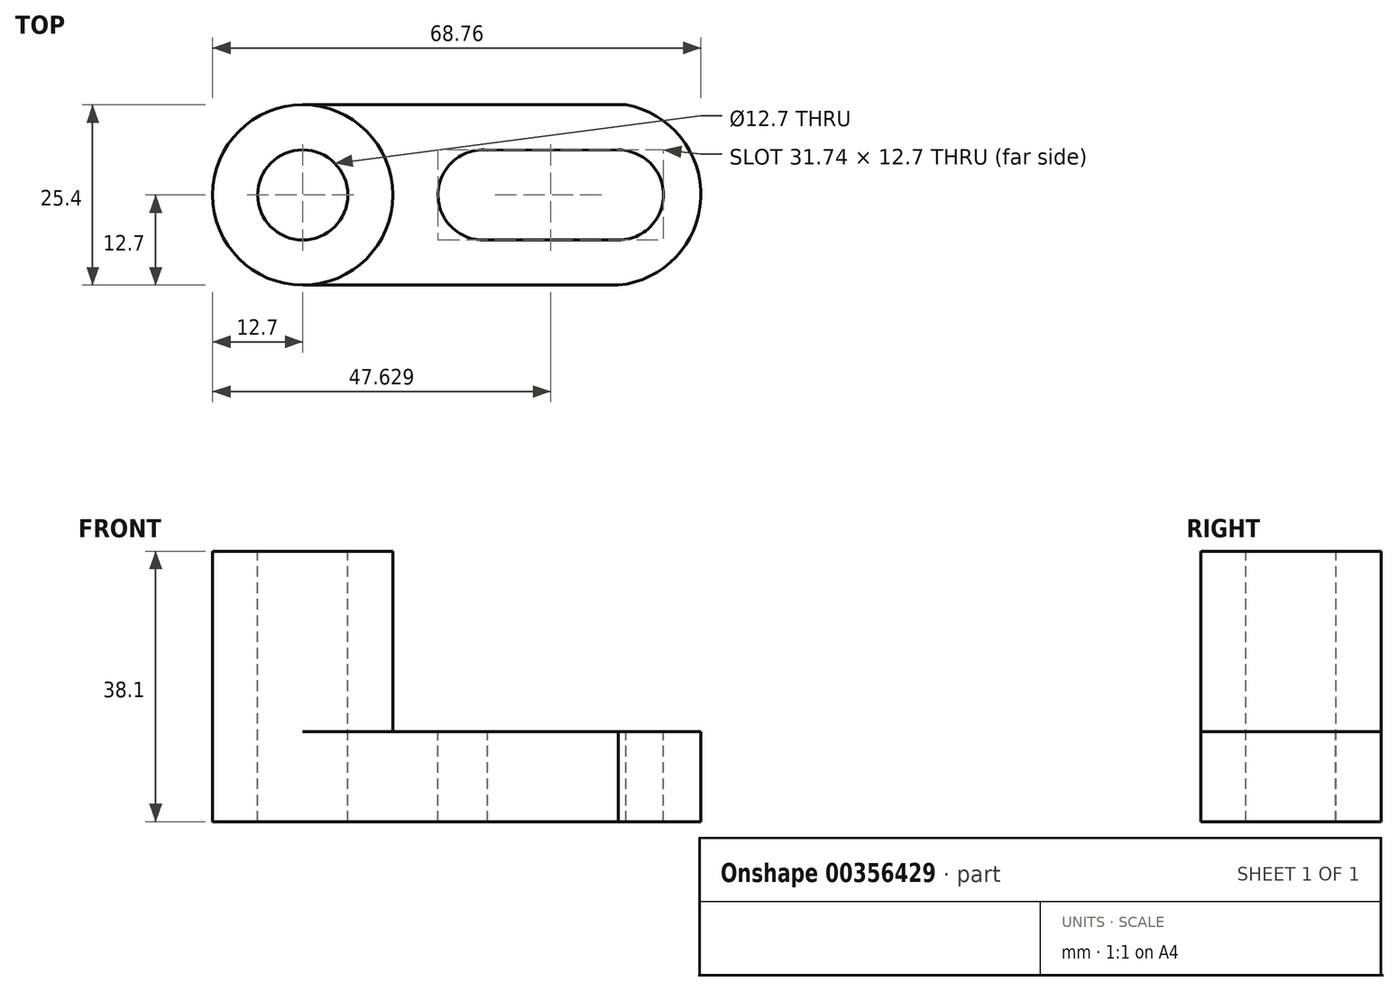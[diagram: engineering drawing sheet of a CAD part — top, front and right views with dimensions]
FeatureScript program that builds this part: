
annotation { "Feature Type Name" : "Feature", "Feature Type Description" : "" }
export const myFeature = defineFeature(function(context is Context, id is Id, definition is map)
    precondition{}
    {
        {
            var Q0;
            Q0=qCreatedBy(makeId("Front.planeOp"),FACE);
            var sketch = newSketch(context, id + "F0", { "sketchPlane" : qUnion([Q0])});
            skLineSegment(sketch, "E0", {"start": v(0, 38.1) * mm, "end": v(0, 0) * mm});
            skLineSegment(sketch, "E1", {"start": v(0, 0) * mm, "end": v(69.85, 0) * mm});
            skLineSegment(sketch, "E2", {"start": v(69.85, 0) * mm, "end": v(69.85, 38.1) * mm});
            skLineSegment(sketch, "E3", {"start": v(69.85, 38.1) * mm, "end": v(0, 38.1) * mm});
            skSolve(sketch);
        }
        {
            var Q0;
            Q0 = qSketchRegion(id + "F0", true);
            extrude(context, id + "F1", {"entities" : qUnion([Q0]), "depth" : 25.4 * mm});
        }
        {
            var Q0;
            Q0=makeQuery(id+"F1.opExtrude","CAP_FACE",FACE,{"disambiguationData":[OSD([sQuery(id+"F0.wireOp",EDGE,"E0"),sQuery(id+"F0.wireOp",EDGE,"E1"),sQuery(id+"F0.wireOp",EDGE,"E2"),sQuery(id+"F0.wireOp",EDGE,"E3")])],"isStart":false});
            var sketch = newSketch(context, id + "F2", { "sketchPlane" : qUnion([Q0])});
            skLineSegment(sketch, "E4", {"start": v(25.4, 38.1) * mm, "end": v(25.4, 12.7) * mm});
            skLineSegment(sketch, "E5", {"start": v(25.4, 12.7) * mm, "end": v(69.85, 12.7) * mm});
            skSolve(sketch);
        }
        {
            var Q0;
            Q0 = qSketchRegion(id + "F2", true);
            var Q1;
            {var subQ0=sQuery(id+"F2.wireOp",EDGE,"E4");Q1=makeQuery(id+"F2.imprint","IMPRINT",FACE,{"disambiguationData":[TD([[makeQuery(id+"F2.imprint","IMPRINT",EDGE,{"derivedFrom":subQ0}),1.0]])]});}
            extrude(context, id + "F3", {"entities" : qUnion([Q0, Q1]), "operationType" : NewBodyOperationType.REMOVE, "oppositeDirection" : true, "depth" : 25.4 * mm});
        }
        {
            var Q0;
            Q0=makeQuery(id+"F1.opExtrude","SWEPT_FACE",FACE,{"disambiguationData":[OSD([sQuery(id+"F0.wireOp",EDGE,"E3")])]});
            var sketch = newSketch(context, id + "F4", { "sketchPlane" : qUnion([Q0])});
            skCircle(sketch, "E6", {"center": v(12.7, -12.7) * mm, "radius": 12.7 * mm});
            skSolve(sketch);
        }
        {
            var Q0;
            {var subQ0=sQuery(id+"F4.wireOp",EDGE,"E6");var subQ1=sQuery(id+"F0.wireOp",EDGE,"E3");var subQ2=makeQuery(id+"F1.opExtrude","CAP_EDGE",EDGE,{"disambiguationData":[OSD([subQ1])],"isStart":true});var subQ3=makeQuery(id+"F4.imprint","INTERSECT",VERTEX,{"derivedFrom":[subQ2,subQ0]});Q0=makeQuery(id+"F4.imprint","IMPRINT",FACE,{"disambiguationData":[TD([[makeQuery(id+"F4.imprint","IMPRINT",EDGE,{"disambiguationData":[TD([[subQ3,-1.0]])],"derivedFrom":subQ0}),-1.0]])]});}
            var Q1;
            {var subQ0=sQuery(id+"F4.wireOp",EDGE,"E6");var subQ1=sQuery(id+"F0.wireOp",EDGE,"E3");var subQ4=makeQuery(id+"F1.opExtrude","CAP_EDGE",EDGE,{"disambiguationData":[OSD([subQ1])],"isStart":false});var subQ5=makeQuery(id+"F4.imprint","INTERSECT",VERTEX,{"derivedFrom":[subQ4,subQ0]});Q1=makeQuery(id+"F4.imprint","IMPRINT",FACE,{"disambiguationData":[TD([[makeQuery(id+"F4.imprint","IMPRINT",EDGE,{"disambiguationData":[TD([[subQ5,1.0]])],"derivedFrom":subQ0}),-1.0]])]});}
            extrude(context, id + "F5", {"entities" : qUnion([Q0, Q1]), "operationType" : NewBodyOperationType.REMOVE, "oppositeDirection" : true, "depth" : 50.8 * mm});
        }
        {
            var Q0;
            Q0=makeQuery(id+"F1.opExtrude","SWEPT_FACE",FACE,{"disambiguationData":[OSD([sQuery(id+"F0.wireOp",EDGE,"E3")])]});
            var sketch = newSketch(context, id + "F6", { "sketchPlane" : qUnion([Q0])});
            skArc(sketch, "E7", {"start": v(12.7, -25.4) * mm, "mid": v(25.4, -12.7) * mm, "end": v(12.7, 0) * mm});
            skSolve(sketch);
        }
        {
            var Q0;
            Q0 = qSketchRegion(id + "F6", true);
            var Q1;
            {var subQ1=sQuery(id+"F0.wireOp",EDGE,"E3");var subQ2=makeQuery(id+"F1.opExtrude","CAP_EDGE",EDGE,{"disambiguationData":[OSD([subQ1])],"isStart":true});var subQ3=subQ2;Q1=makeQuery(id+"F6.imprint","IMPRINT",FACE,{"disambiguationData":[TD([[makeQuery(id+"F6.imprint","IMPRINT",EDGE,{"derivedFrom":subQ3}),1.0]])]});}
            var Q2;
            {var subQ1=sQuery(id+"F0.wireOp",EDGE,"E3");var subQ2=makeQuery(id+"F1.opExtrude","CAP_EDGE",EDGE,{"disambiguationData":[OSD([subQ1])],"isStart":false});var subQ3=subQ2;Q2=makeQuery(id+"F6.imprint","IMPRINT",FACE,{"disambiguationData":[TD([[makeQuery(id+"F6.imprint","IMPRINT",EDGE,{"derivedFrom":subQ3}),-1.0]])]});}
            extrude(context, id + "F7", {"entities" : qUnion([Q0, Q1, Q2]), "operationType" : NewBodyOperationType.REMOVE, "oppositeDirection" : true, "depth" : 25.4 * mm});
        }
        {
            var Q0;
            Q0=makeQuery(id+"F1.opExtrude","SWEPT_FACE",FACE,{"disambiguationData":[OSD([sQuery(id+"F0.wireOp",EDGE,"E3")])]});
            var sketch = newSketch(context, id + "F8", { "sketchPlane" : qUnion([Q0])});
            skCircle(sketch, "E8", {"center": v(12.7, -12.7) * mm, "radius": 6.35 * mm});
            skSolve(sketch);
        }
        {
            var Q0;
            Q0=makeQuery(id+"F8.imprint","IMPRINT",FACE,{"disambiguationData":[TD([[makeQuery(id+"F8.imprint","IMPRINT",EDGE,{"derivedFrom":sQuery(id+"F8.wireOp",EDGE,"E8")}),1.0]])]});
            extrude(context, id + "F9", {"entities" : qUnion([Q0]), "operationType" : NewBodyOperationType.REMOVE, "oppositeDirection" : true, "depth" : 50.8 * mm});
        }
        {
            var Q0;
            {var subQ0=sQuery(id+"F0.wireOp",EDGE,"E3");var subQ1=makeQuery(id+"F1.opExtrude","CAP_EDGE",EDGE,{"disambiguationData":[OSD([subQ0])],"isStart":true});var subQ2=subQ1;var subQ3=sQuery(id+"F2.wireOp",EDGE,"E4");var subQ4=makeQuery(id+"F3.boolean.opBoolean","COPY",EDGE,{"derivedFrom":makeQuery(id+"F3.opExtrude","SWEPT_EDGE",EDGE,{"disambiguationData":[OSD([subQ0,subQ3])]})});var subQ5=sQuery(id+"F6.wireOp",EDGE,"E7");var subQ6=makeQuery(id+"F6.imprint","INTERSECT",VERTEX,{"derivedFrom":[subQ4,subQ5]});var subQ9=makeQuery(id+"F1.opExtrude","CAP_EDGE",EDGE,{"disambiguationData":[OSD([subQ0])],"isStart":false});var subQ11=subQ9;Q0=makeQuery(id+"F7.boolean.opBoolean","MERGE",FACE,{"derivedFrom":[makeQuery(id+"F3.boolean.opBoolean","COPY",FACE,{"derivedFrom":makeQuery(id+"F3.opExtrude","SWEPT_FACE",FACE,{"disambiguationData":[OSD([sQuery(id+"F2.wireOp",EDGE,"E5")])]})}),makeQuery(id+"F7.opExtrude","CAP_FACE",FACE,{"disambiguationData":[OSD([subQ0,subQ3,subQ5]),TDD([makeQuery(id+"F6.imprint","IMPRINT",EDGE,{"disambiguationData":[TD([[subQ6,1.0]])],"derivedFrom":subQ5}),makeQuery(id+"F6.imprint","IMPRINT",EDGE,{"derivedFrom":subQ11}),makeQuery(id+"F6.imprint","IMPRINT",EDGE,{"disambiguationData":[TD([[makeQuery(id+"F6.imprint","INTERSECT",VERTEX,{"derivedFrom":[subQ4,subQ11]}),1.0]])],"derivedFrom":subQ4})])],"isStart":false}),makeQuery(id+"F7.opExtrude","CAP_FACE",FACE,{"disambiguationData":[OSD([subQ0,subQ3,subQ5]),TDD([makeQuery(id+"F6.imprint","IMPRINT",EDGE,{"disambiguationData":[TD([[subQ6,-1.0]])],"derivedFrom":subQ5}),makeQuery(id+"F6.imprint","IMPRINT",EDGE,{"derivedFrom":subQ2}),makeQuery(id+"F6.imprint","IMPRINT",EDGE,{"disambiguationData":[TD([[makeQuery(id+"F6.imprint","INTERSECT",VERTEX,{"derivedFrom":[subQ4,subQ2]}),-1.0]])],"derivedFrom":subQ4})])],"isStart":false})]});}
            var sketch = newSketch(context, id + "F10", { "sketchPlane" : qUnion([Q0])});
            skCircle(sketch, "E9", {"center": v(38.1, -12.7) * mm, "radius": 6.35 * mm});
            skCircle(sketch, "E10", {"center": v(57.15, -12.7) * mm, "radius": 6.35 * mm});
            skLineSegment(sketch, "E11", {"start": v(38.7, -6.38) * mm, "end": v(57.14, -6.35) * mm});
            skLineSegment(sketch, "E12", {"start": v(57.14, -6.35) * mm, "end": v(57.15, -19.05) * mm});
            skLineSegment(sketch, "E13", {"start": v(57.15, -19.05) * mm, "end": v(38.1, -19.05) * mm});
            skLineSegment(sketch, "E14", {"start": v(38.1, -19.05) * mm, "end": v(38.7, -6.38) * mm});
            skSolve(sketch);
        }
        {
            var Q0;
            Q0 = qSketchRegion(id + "F10", true);
            extrude(context, id + "F11", {"entities" : qUnion([Q0]), "operationType" : NewBodyOperationType.REMOVE, "oppositeDirection" : true, "depth" : 25.4 * mm});
        }
        {
            var Q0;
            {var subQ0=sQuery(id+"F0.wireOp",EDGE,"E3");var subQ1=makeQuery(id+"F1.opExtrude","CAP_EDGE",EDGE,{"disambiguationData":[OSD([subQ0])],"isStart":true});var subQ2=subQ1;var subQ3=sQuery(id+"F2.wireOp",EDGE,"E4");var subQ4=makeQuery(id+"F3.boolean.opBoolean","COPY",EDGE,{"derivedFrom":makeQuery(id+"F3.opExtrude","SWEPT_EDGE",EDGE,{"disambiguationData":[OSD([subQ0,subQ3])]})});var subQ5=sQuery(id+"F6.wireOp",EDGE,"E7");var subQ6=makeQuery(id+"F6.imprint","INTERSECT",VERTEX,{"derivedFrom":[subQ4,subQ5]});var subQ9=makeQuery(id+"F1.opExtrude","CAP_EDGE",EDGE,{"disambiguationData":[OSD([subQ0])],"isStart":false});var subQ11=subQ9;Q0=makeQuery(id+"F7.boolean.opBoolean","MERGE",FACE,{"derivedFrom":[makeQuery(id+"F3.boolean.opBoolean","COPY",FACE,{"derivedFrom":makeQuery(id+"F3.opExtrude","SWEPT_FACE",FACE,{"disambiguationData":[OSD([sQuery(id+"F2.wireOp",EDGE,"E5")])]})}),makeQuery(id+"F7.opExtrude","CAP_FACE",FACE,{"disambiguationData":[OSD([subQ0,subQ3,subQ5]),TDD([makeQuery(id+"F6.imprint","IMPRINT",EDGE,{"disambiguationData":[TD([[subQ6,1.0]])],"derivedFrom":subQ5}),makeQuery(id+"F6.imprint","IMPRINT",EDGE,{"derivedFrom":subQ11}),makeQuery(id+"F6.imprint","IMPRINT",EDGE,{"disambiguationData":[TD([[makeQuery(id+"F6.imprint","INTERSECT",VERTEX,{"derivedFrom":[subQ4,subQ11]}),1.0]])],"derivedFrom":subQ4})])],"isStart":false}),makeQuery(id+"F7.opExtrude","CAP_FACE",FACE,{"disambiguationData":[OSD([subQ0,subQ3,subQ5]),TDD([makeQuery(id+"F6.imprint","IMPRINT",EDGE,{"disambiguationData":[TD([[subQ6,-1.0]])],"derivedFrom":subQ5}),makeQuery(id+"F6.imprint","IMPRINT",EDGE,{"derivedFrom":subQ2}),makeQuery(id+"F6.imprint","IMPRINT",EDGE,{"disambiguationData":[TD([[makeQuery(id+"F6.imprint","INTERSECT",VERTEX,{"derivedFrom":[subQ4,subQ2]}),-1.0]])],"derivedFrom":subQ4})])],"isStart":false})]});}
            var sketch = newSketch(context, id + "F12", { "sketchPlane" : qUnion([Q0])});
            skArc(sketch, "E15", {"start": v(57.14, -25.4) * mm, "mid": v(68.75, -13.16) * mm, "end": v(58.19, 0) * mm});
            skSolve(sketch);
        }
        {
            var Q0;
            Q0 = qSketchRegion(id + "F12", true);
            var Q1;
            {var subQ0=sQuery(id+"F12.wireOp",EDGE,"E15");Q1=makeQuery(id+"F12.imprint","IMPRINT",FACE,{"disambiguationData":[TD([[makeQuery(id+"F12.imprint","IMPRINT",EDGE,{"derivedFrom":subQ0}),-1.0]])]});}
            extrude(context, id + "F13", {"entities" : qUnion([Q0, Q1]), "operationType" : NewBodyOperationType.REMOVE, "oppositeDirection" : true, "depth" : 25.4 * mm});
        }
    });
